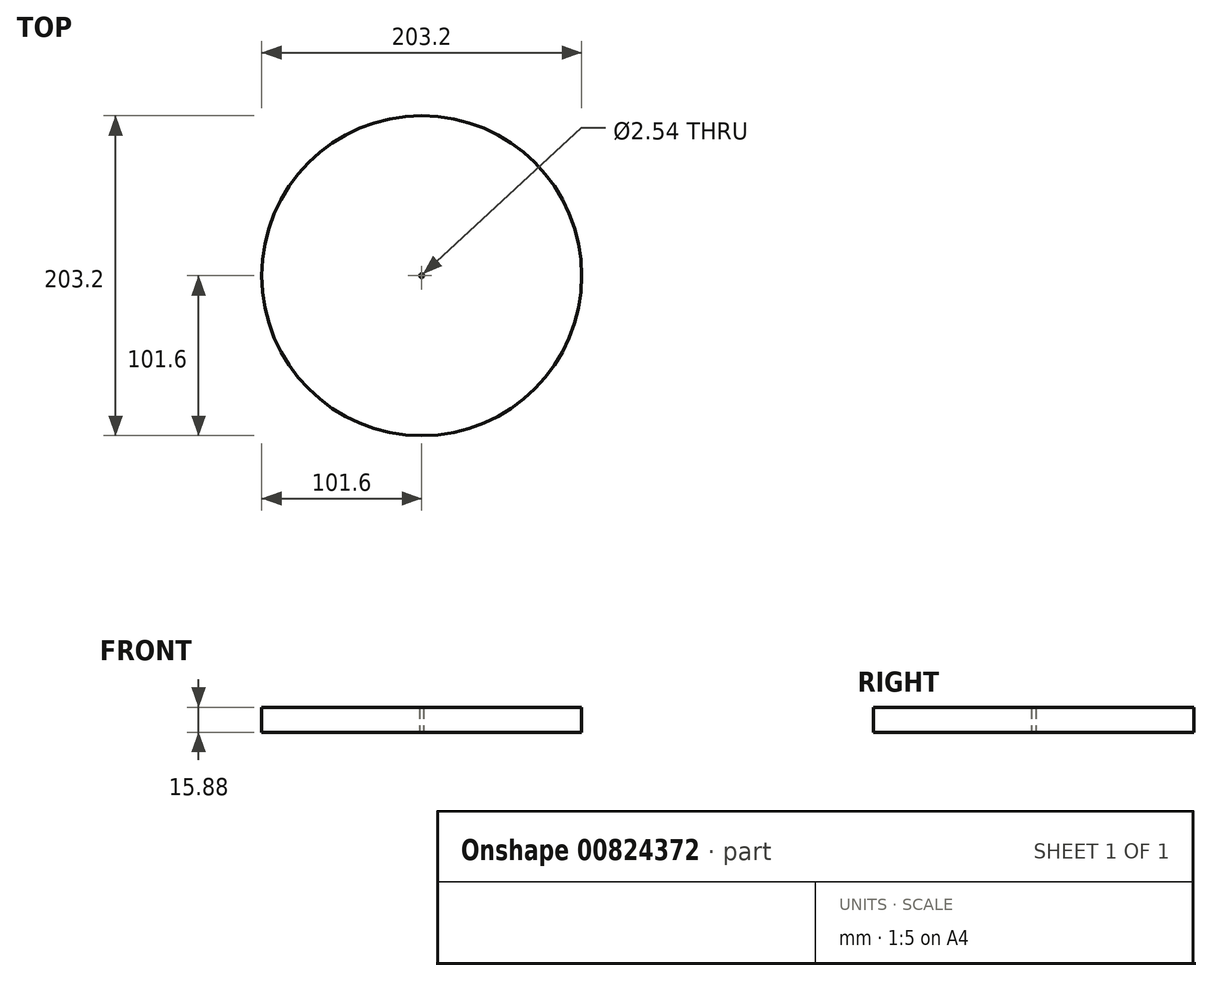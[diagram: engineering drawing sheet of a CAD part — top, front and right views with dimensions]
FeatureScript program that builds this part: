
annotation { "Feature Type Name" : "Feature", "Feature Type Description" : "" }
export const myFeature = defineFeature(function(context is Context, id is Id, definition is map)
    precondition{}
    {
        {
            var Q0;
            Q0=qCreatedBy(makeId("Top.planeOp"),FACE);
            var sketch = newSketch(context, id + "F0", { "sketchPlane" : qUnion([Q0])});
            skCircle(sketch, "E0", {"center": v(0, 0) * mm, "radius": 101.6 * mm});
            skCircle(sketch, "E1", {"center": v(0, 0) * mm, "radius": 1.27 * mm});
            skSolve(sketch);
        }
        {
            var Q0;
            Q0=makeQuery(id+"F0.imprint","IMPRINT",FACE,{"disambiguationData":[TD([[makeQuery(id+"F0.imprint","IMPRINT",EDGE,{"derivedFrom":sQuery(id+"F0.wireOp",EDGE,"E0")}),1.0]])]});
            extrude(context, id + "F1", {"entities" : qUnion([Q0]), "depth" : 15.88 * mm, "offsetDistance" : 25.4 * mm});
        }
    });
